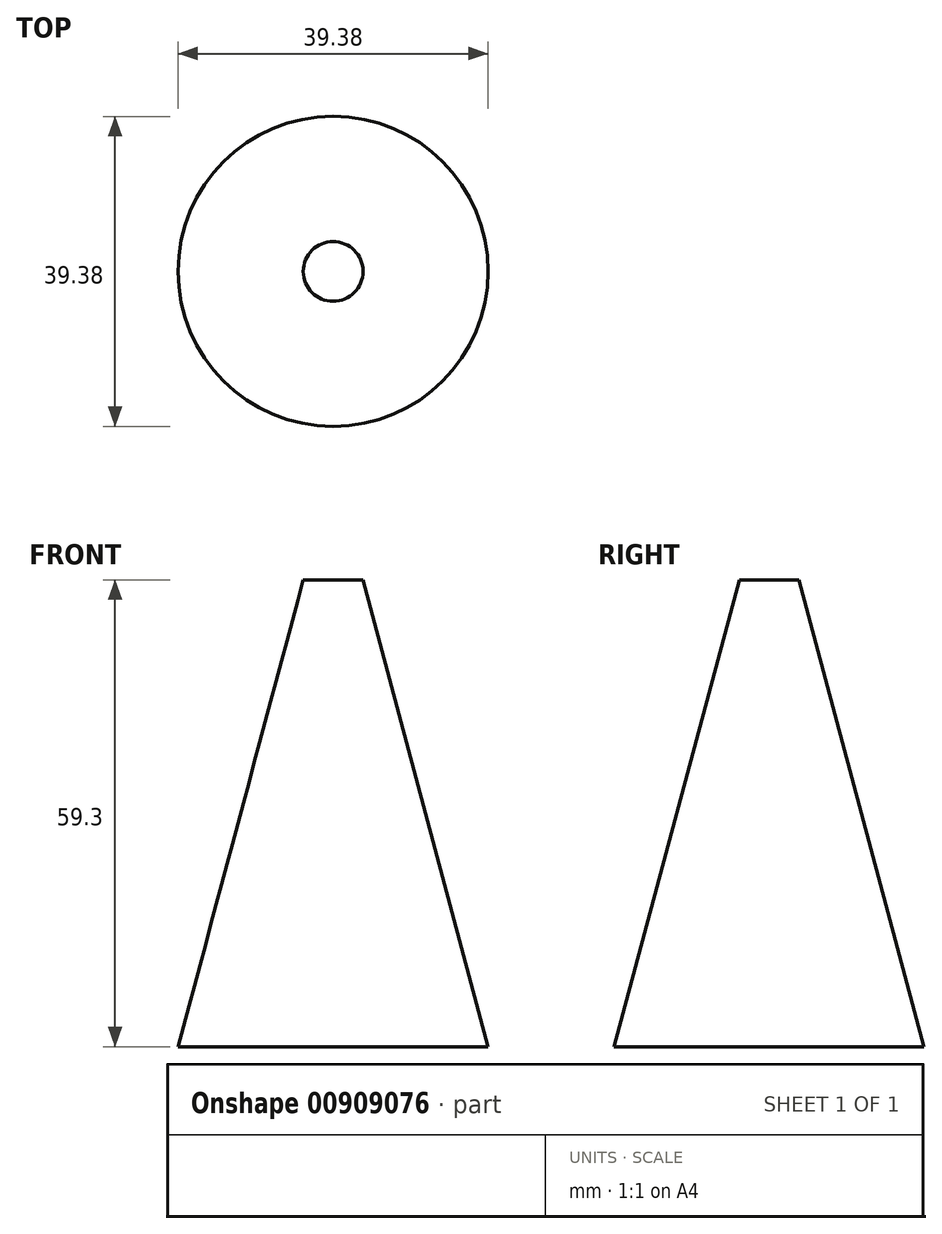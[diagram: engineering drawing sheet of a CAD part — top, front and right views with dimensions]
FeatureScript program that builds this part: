
annotation { "Feature Type Name" : "Feature", "Feature Type Description" : "" }
export const myFeature = defineFeature(function(context is Context, id is Id, definition is map)
    precondition{}
    {
        {
            var Q0;
            Q0=qCreatedBy(makeId("Front.planeOp"),FACE);
            var sketch = newSketch(context, id + "F0", { "sketchPlane" : qUnion([Q0])});
            skLineSegment(sketch, "E0", {"start": v(0, 59.3) * mm, "end": v(3.8, 59.3) * mm});
            skLineSegment(sketch, "E1", {"start": v(3.8, 59.3) * mm, "end": v(19.7, 0) * mm});
            skLineSegment(sketch, "E2", {"start": v(19.7, 0) * mm, "end": v(0, 0) * mm});
            skLineSegment(sketch, "E3", {"start": v(0, 0) * mm, "end": v(0, 59.3) * mm});
            skSolve(sketch);
        }
        {
            var Q0;
            Q0 = qSketchRegion(id + "F0", true);
            var Q1;
            Q1=sQuery(id+"F0.wireOp",EDGE,"E3");
            revolve(context, id + "F1", {"surfaceOperationType" : NewSurfaceOperationType.NEW, "entities" : qUnion([Q0]), "axis" : qUnion([Q1]), "revolveType" : RevolveType.FULL});
        }
    });
